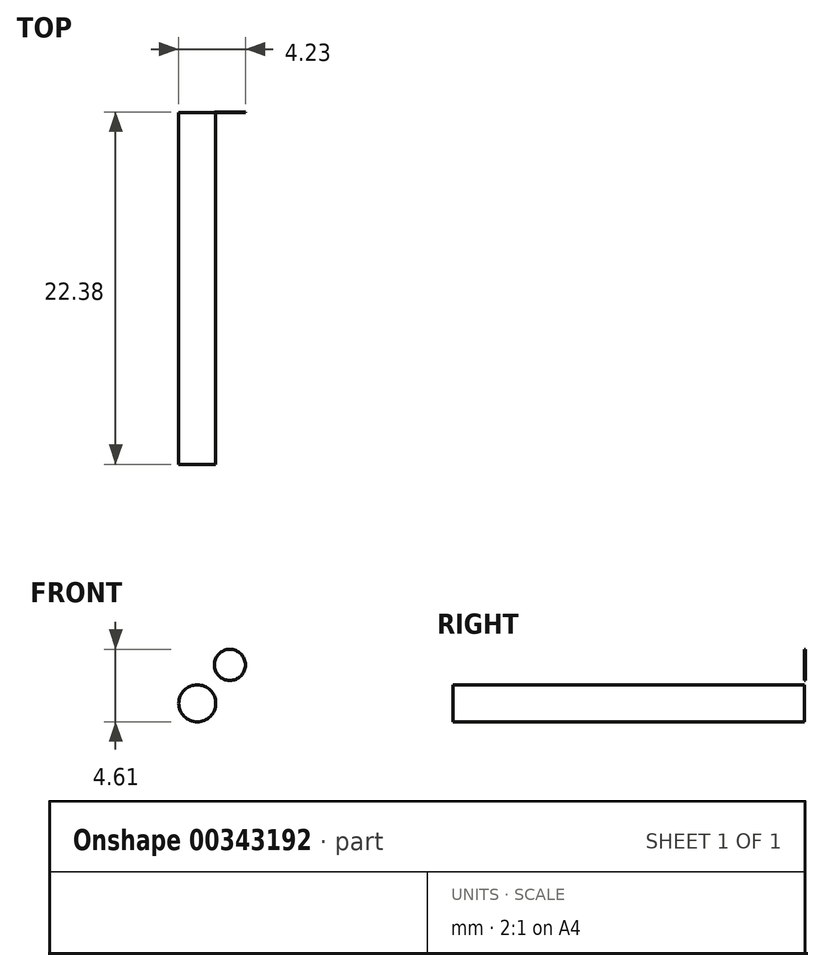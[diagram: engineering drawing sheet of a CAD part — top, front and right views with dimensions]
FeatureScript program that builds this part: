
annotation { "Feature Type Name" : "Feature", "Feature Type Description" : "" }
export const myFeature = defineFeature(function(context is Context, id is Id, definition is map)
    precondition{}
    {
        {
            var Q0;
            Q0=qCreatedBy(makeId("Front.planeOp"),FACE);
            var sketch = newSketch(context, id + "F0", { "sketchPlane" : qUnion([Q0])});
            skCircle(sketch, "E0", {"center": v(6.52, 8.9) * mm, "radius": 1.18 * mm});
            skSolve(sketch);
        }
        {
            var Q0;
            Q0 = qSketchRegion(id + "F0", true);
            extrude(context, id + "F1", {"entities" : qUnion([Q0]), "depth" : 22.33 * mm});
        }
        {
            var Q0;
            Q0=makeQuery(id+"F0.imprint","IMPRINT",FACE,{"disambiguationData":[TD([[makeQuery(id+"F0.imprint","IMPRINT",EDGE,{"derivedFrom":sQuery(id+"F0.wireOp",EDGE,"E0")}),1.0]])]});
            var sketch = newSketch(context, id + "F2", { "sketchPlane" : qUnion([Q0])});
            skCircle(sketch, "E1", {"center": v(8.6, 11.35) * mm, "radius": 0.99 * mm});
            skSolve(sketch);
        }
        {
            var Q0;
            Q0 = qSketchRegion(id + "F2", true);
            extrude(context, id + "F3", {"entities" : qUnion([Q0]), "oppositeDirection" : true, "depth" : 0.05 * mm});
        }
    });
